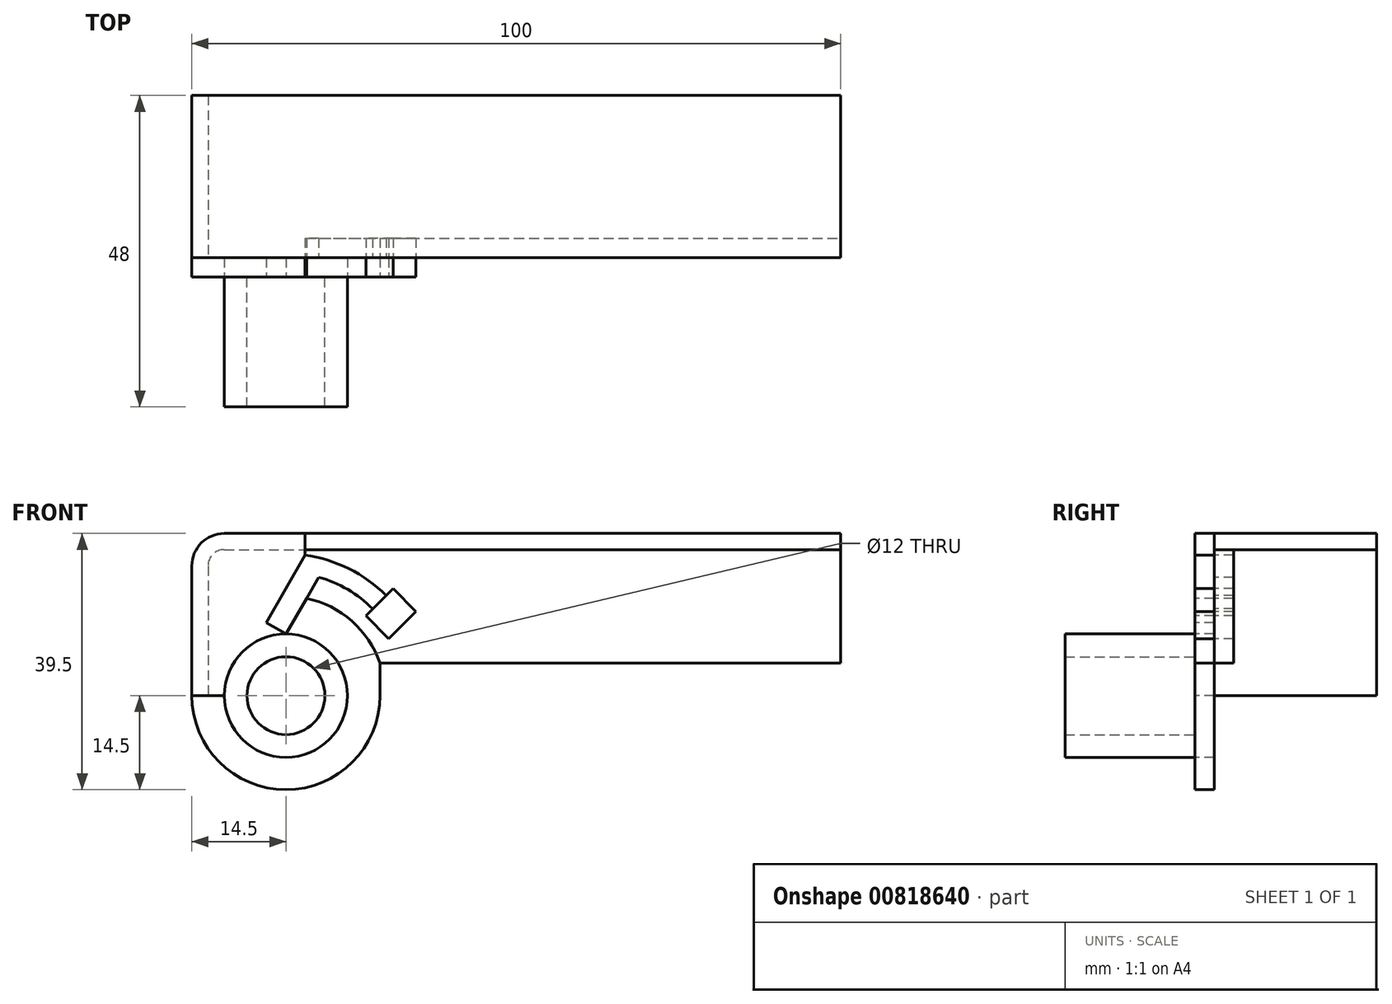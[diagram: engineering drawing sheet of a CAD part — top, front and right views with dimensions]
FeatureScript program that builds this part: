
annotation { "Feature Type Name" : "Feature", "Feature Type Description" : "" }
export const myFeature = defineFeature(function(context is Context, id is Id, definition is map)
    precondition{}
    {
        {
            var Q0;
            Q0=qCreatedBy(makeId("Front.planeOp"),FACE);
            var sketch = newSketch(context, id + "F0", { "sketchPlane" : qUnion([Q0])});
            skCircle(sketch, "E0", {"center": v(0, 0) * mm, "radius": 6 * mm});
            skCircle(sketch, "E1", {"center": v(0, 0) * mm, "radius": 9.5 * mm});
            skLineSegment(sketch, "E2", {"start": v(0, 0) * mm, "end": v(-14.5, 0) * mm, "construction": true});
            skLineSegment(sketch, "E3", {"start": v(-14.5, 0) * mm, "end": v(-14.5, 69.12) * mm, "construction": true});
            skPoint(sketch, "E4", {"position": v(-14.5, 25) * mm});
            skLineSegment(sketch, "E5", {"start": v(-45.8, 25) * mm, "end": v(91.74, 25) * mm, "construction": true});
            skLineSegment(sketch, "E6", {"start": v(0, 54.9) * mm, "end": v(0, -39.4) * mm, "construction": true});
            skLineSegment(sketch, "E7", {"start": v(-46.64, 0) * mm, "end": v(89.6, 0) * mm, "construction": true});
            skLineSegment(sketch, "E8.MirrorCS", {"start": v(14.5, 0) * mm, "end": v(14.5, 69.12) * mm, "construction": true});
            skPoint(sketch, "E9", {"position": v(14.5, 5) * mm});
            skLineSegment(sketch, "E10", {"start": v(14.5, 5) * mm, "end": v(89.89, 5) * mm, "construction": true});
            skArc(sketch, "E11", {"start": v(-14.5, 0) * mm, "mid": v(0, -14.5) * mm, "end": v(14.5, 0) * mm});
            skLineSegment(sketch, "E12", {"start": v(14.5, 0) * mm, "end": v(14.5, 5) * mm});
            skLineSegment(sketch, "E13", {"start": v(-14.5, 0) * mm, "end": v(-14.5, 25) * mm});
            skLineSegment(sketch, "E14", {"start": v(-14.5, 25) * mm, "end": v(85.5, 25) * mm});
            skLineSegment(sketch, "E15", {"start": v(85.5, 30.33) * mm, "end": v(85.5, -4.62) * mm, "construction": true});
            skLineSegment(sketch, "E16", {"start": v(14.5, 5) * mm, "end": v(85.5, 5) * mm});
            skPoint(sketch, "E17", {"position": v(5.5, 25) * mm});
            skLineSegment(sketch, "E18", {"start": v(0, 9.5) * mm, "end": v(-3.03, 11.25) * mm});
            skLineSegment(sketch, "E19", {"start": v(-3.03, 11.25) * mm, "end": v(2.97, 21.64) * mm});
            skArc(sketch, "E20", {"start": v(2.97, 21.64) * mm, "mid": v(9.71, 19.57) * mm, "end": v(15.45, 15.45) * mm});
            skLineSegment(sketch, "E21", {"start": v(15.45, 15.45) * mm, "end": v(0, 0) * mm, "construction": true});
            skPoint(sketch, "E22", {"position": v(6.55, 20.84) * mm});
            skPoint(sketch, "E23", {"position": v(5.05, 18.24) * mm});
            skArc(sketch, "E24", {"start": v(5.05, 18.24) * mm, "mid": v(9.53, 16.35) * mm, "end": v(13.38, 13.38) * mm});
            skLineSegment(sketch, "E25", {"start": v(5.05, 18.24) * mm, "end": v(0, 9.5) * mm});
            skLineSegment(sketch, "E26", {"start": v(15.45, 15.45) * mm, "end": v(13.38, 13.38) * mm});
            skArc(sketch, "E27", {"start": v(14.5, 5) * mm, "mid": v(10.16, 11.5) * mm, "end": v(3.18, 15) * mm});
            skLineSegment(sketch, "E28", {"start": v(15.45, 15.45) * mm, "end": v(16.5, 16.5) * mm});
            skLineSegment(sketch, "E29", {"start": v(16.5, 16.5) * mm, "end": v(20.04, 12.97) * mm});
            skLineSegment(sketch, "E30", {"start": v(20.04, 12.97) * mm, "end": v(15.86, 8.79) * mm});
            skLineSegment(sketch, "E31", {"start": v(15.86, 8.79) * mm, "end": v(12.32, 12.32) * mm});
            skLineSegment(sketch, "E32", {"start": v(13.38, 13.38) * mm, "end": v(12.32, 12.32) * mm});
            skLineSegment(sketch, "E33", {"start": v(14.5, 5) * mm, "end": v(8.08, 5) * mm});
            skLineSegment(sketch, "E34", {"start": v(-14.5, 0) * mm, "end": v(-9.5, 0) * mm});
            skLineSegment(sketch, "E35", {"start": v(2.97, 21.64) * mm, "end": v(2.97, 25) * mm});
            skLineSegment(sketch, "E36", {"start": v(85.5, 5) * mm, "end": v(85.5, 25) * mm});
            skLineSegment(sketch, "E37", {"start": v(-14.5, 20) * mm, "end": v(-49.67, 20) * mm, "construction": true});
            skLineSegment(sketch, "E38", {"start": v(-14.5, 20) * mm, "end": v(-4.5, 20) * mm, "construction": true});
            skLineSegment(sketch, "E39", {"start": v(-9.5, 20) * mm, "end": v(-9.5, 42.7) * mm, "construction": true});
            skArc(sketch, "E40", {"start": v(-14.5, 20) * mm, "mid": v(-13.04, 23.54) * mm, "end": v(-9.5, 25) * mm});
            skSolve(sketch);
        }
        {
            var Q0;
            Q0=makeQuery(id+"F0.imprint","IMPRINT",FACE,{"disambiguationData":[TD([[makeQuery(id+"F0.imprint","IMPRINT",EDGE,{"derivedFrom":sQuery(id+"F0.wireOp",EDGE,"E0")}),-1.0]])]});
            extrude(context, id + "F1", {"entities" : qUnion([Q0]), "depth" : 20 * mm, "offsetDistance" : 25 * mm});
        }
        {
            var Q0;
            {var subQ4=sQuery(id+"F0.wireOp",EDGE,"E27");Q0=makeQuery(id+"F0.imprint","IMPRINT",FACE,{"disambiguationData":[TD([[makeQuery(id+"F0.imprint","IMPRINT",EDGE,{"derivedFrom":subQ4}),1.0]])]});}
            var Q1;
            Q1=makeQuery(id+"F0.imprint","IMPRINT",FACE,{"disambiguationData":[TD([[makeQuery(id+"F0.imprint","IMPRINT",EDGE,{"derivedFrom":sQuery(id+"F0.wireOp",EDGE,"E11")}),1.0]])]});
            extrude(context, id + "F2", {"entities" : qUnion([Q0, Q1]), "oppositeDirection" : true, "depth" : 3 * mm, "offsetDistance" : 25 * mm});
        }
        {
            var Q0;
            {var subQ5=sQuery(id+"F0.wireOp",EDGE,"E18");Q0=makeQuery(id+"F0.imprint","IMPRINT",FACE,{"disambiguationData":[TD([[makeQuery(id+"F0.imprint","IMPRINT",EDGE,{"derivedFrom":subQ5}),1.0]])]});}
            extrude(context, id + "F3", {"entities" : qUnion([Q0]), "oppositeDirection" : true, "depth" : 3 * mm, "offsetDistance" : 25 * mm});
        }
        {
            var Q0;
            Q0=makeQuery(id+"F0.imprint","IMPRINT",FACE,{"disambiguationData":[TD([[makeQuery(id+"F0.imprint","IMPRINT",EDGE,{"derivedFrom":sQuery(id+"F0.wireOp",EDGE,"E26")}),1.0]])]});
            var Q1;
            Q1=makeQuery(id+"F2.opExtrude","CAP_FACE",FACE,{"disambiguationData":[OSD([sQuery(id+"F0.wireOp",EDGE,"E1"),sQuery(id+"F0.wireOp",EDGE,"E11"),sQuery(id+"F0.wireOp",EDGE,"E12"),sQuery(id+"F0.wireOp",EDGE,"E25"),sQuery(id+"F0.wireOp",EDGE,"E27"),sQuery(id+"F0.wireOp",EDGE,"E34")])],"isStart":false});
            extrude(context, id + "F4", {"entities" : qUnion([Q0]), "operationType" : NewBodyOperationType.ADD, "endBound" : BoundingType.UP_TO_SURFACE, "oppositeDirection" : true, "depth" : 3 * mm, "endBoundEntityFace" : qUnion([Q1]), "offsetDistance" : 25 * mm});
        }
        {
            var Q0;
            Q0=makeQuery(id+"F3.opExtrude","CAP_FACE",FACE,{"disambiguationData":[OSD([sQuery(id+"F0.wireOp",EDGE,"E13"),sQuery(id+"F0.wireOp",EDGE,"E14"),sQuery(id+"F0.wireOp",EDGE,"E40")])],"isStart":false});
            var sketch = newSketch(context, id + "F5", { "sketchPlane" : qUnion([Q0])});
            skArc(sketch, "E41.0.0", {"start": v(-3.18, 15) * mm, "mid": v(-10.16, 11.5) * mm, "end": v(-14.5, 5) * mm});
            skLineSegment(sketch, "E41.0.1", {"start": v(-14.5, 5) * mm, "end": v(-85.5, 5) * mm});
            skLineSegment(sketch, "E41.0.2", {"start": v(-85.5, 5) * mm, "end": v(-85.5, 25) * mm});
            skLineSegment(sketch, "E41.0.3", {"start": v(-85.5, 25) * mm, "end": v(-2.97, 25) * mm});
            skLineSegment(sketch, "E41.0.4", {"start": v(-2.97, 25) * mm, "end": v(-2.97, 21.64) * mm});
            skArc(sketch, "E41.0.5", {"start": v(-2.97, 21.64) * mm, "mid": v(-9.71, 19.57) * mm, "end": v(-15.45, 15.45) * mm});
            skLineSegment(sketch, "E41.0.6", {"start": v(-15.45, 15.45) * mm, "end": v(-16.5, 16.5) * mm});
            skLineSegment(sketch, "E41.0.7", {"start": v(-16.5, 16.5) * mm, "end": v(-20.04, 12.97) * mm});
            skLineSegment(sketch, "E41.0.8", {"start": v(-20.04, 12.97) * mm, "end": v(-15.86, 8.79) * mm});
            skLineSegment(sketch, "E41.0.9", {"start": v(-15.86, 8.79) * mm, "end": v(-12.32, 12.32) * mm});
            skLineSegment(sketch, "E41.0.10", {"start": v(-12.32, 12.32) * mm, "end": v(-13.38, 13.38) * mm});
            skArc(sketch, "E41.0.11", {"start": v(-13.38, 13.38) * mm, "mid": v(-9.53, 16.35) * mm, "end": v(-5.05, 18.24) * mm});
            skLineSegment(sketch, "E41.0.12", {"start": v(-5.05, 18.24) * mm, "end": v(-3.18, 15) * mm});
            skLineSegment(sketch, "E42", {"start": v(-2.97, 25) * mm, "end": v(-2.97, 27.86) * mm, "construction": true});
            skLineSegment(sketch, "E43", {"start": v(-5.97, 25) * mm, "end": v(-5.97, 28.12) * mm, "construction": true});
            skLineSegment(sketch, "E44", {"start": v(-5.97, 25) * mm, "end": v(3.27, 0) * mm, "construction": true});
            skPoint(sketch, "E44.endSnap0", {"position": v(3.27, 25) * mm});
            skLineSegment(sketch, "E45", {"start": v(12, 20) * mm, "end": v(12, 0) * mm});
            skArc(sketch, "E46", {"start": v(12, 20) * mm, "mid": v(11.27, 21.77) * mm, "end": v(9.5, 22.5) * mm});
            skLineSegment(sketch, "E47", {"start": v(9.5, 22.5) * mm, "end": v(-85.5, 22.5) * mm});
            skSolve(sketch);
        }
        {
            var Q0;
            Q0=makeQuery(id+"F5.imprint","IMPRINT",FACE,{"disambiguationData":[TD([[makeQuery(id+"F5.imprint","IMPRINT",EDGE,{"derivedFrom":sQuery(id+"F5.wireOp",EDGE,"E41.0.0")}),-1.0]])]});
            extrude(context, id + "F6", {"entities" : qUnion([Q0]), "depth" : 3 * mm, "offsetDistance" : 25 * mm});
        }
        {
            var Q0;
            {var subQ0=sQuery(id+"F5.wireOp",EDGE,"E41.0.3");Q0=makeQuery(id+"F5.imprint","IMPRINT",FACE,{"disambiguationData":[TD([[makeQuery(id+"F5.imprint","IMPRINT",EDGE,{"derivedFrom":subQ0}),-1.0]])]});}
            var Q1;
            {var subQ5=sQuery(id+"F5.wireOp",EDGE,"E45");Q1=makeQuery(id+"F5.imprint","IMPRINT",FACE,{"disambiguationData":[TD([[makeQuery(id+"F5.imprint","IMPRINT",EDGE,{"derivedFrom":subQ5}),1.0]])]});}
            extrude(context, id + "F7", {"entities" : qUnion([Q0, Q1]), "depth" : 25 * mm, "offsetDistance" : 25 * mm});
        }
        {
            var Q0;
            Q0=makeQuery(id+"F4.opExtrude","CAP_FACE",FACE,{"disambiguationData":[OSD([sQuery(id+"F0.wireOp",EDGE,"E26"),sQuery(id+"F0.wireOp",EDGE,"E28"),sQuery(id+"F0.wireOp",EDGE,"E29"),sQuery(id+"F0.wireOp",EDGE,"E30"),sQuery(id+"F0.wireOp",EDGE,"E31"),sQuery(id+"F0.wireOp",EDGE,"E32")])],"isStart":false});
            var Q1;
            Q1=makeQuery(id+"F6.opExtrude","CAP_FACE",FACE,{"disambiguationData":[OSD([sQuery(id+"F5.wireOp",EDGE,"E41.0.0"),sQuery(id+"F5.wireOp",EDGE,"E41.0.1"),sQuery(id+"F5.wireOp",EDGE,"E41.0.2"),sQuery(id+"F5.wireOp",EDGE,"E41.0.4"),sQuery(id+"F5.wireOp",EDGE,"E41.0.5"),sQuery(id+"F5.wireOp",EDGE,"E41.0.6"),sQuery(id+"F5.wireOp",EDGE,"E41.0.7"),sQuery(id+"F5.wireOp",EDGE,"E41.0.8"),sQuery(id+"F5.wireOp",EDGE,"E41.0.9"),sQuery(id+"F5.wireOp",EDGE,"E41.0.10"),sQuery(id+"F5.wireOp",EDGE,"E41.0.11"),sQuery(id+"F5.wireOp",EDGE,"E41.0.12"),sQuery(id+"F5.wireOp",EDGE,"E47")])],"isStart":false});
            extrude(context, id + "F8", {"entities" : qUnion([Q0]), "endBound" : BoundingType.UP_TO_SURFACE, "depth" : 25 * mm, "endBoundEntityFace" : qUnion([Q1]), "offsetDistance" : 25 * mm});
        }
    });
